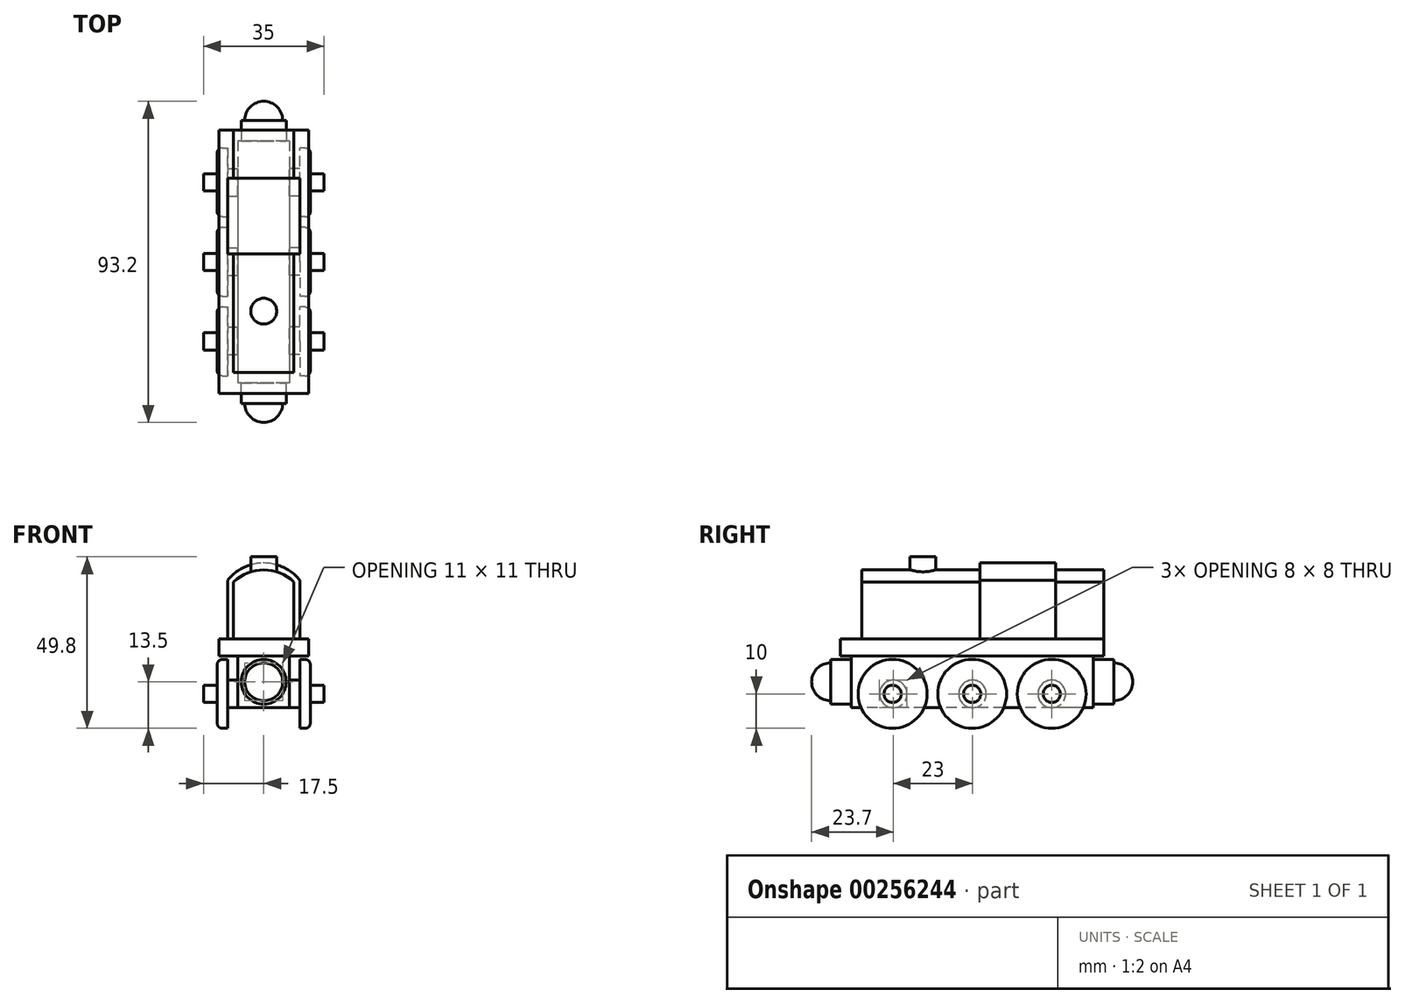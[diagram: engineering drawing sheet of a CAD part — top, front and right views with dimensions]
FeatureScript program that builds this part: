
annotation { "Feature Type Name" : "Feature", "Feature Type Description" : "" }
export const myFeature = defineFeature(function(context is Context, id is Id, definition is map)
    precondition{}
    {
        {
            var Q0;
            Q0=qCreatedBy(makeId("Front.planeOp"),FACE);
            var sketch = newSketch(context, id + "F0", { "sketchPlane" : qUnion([Q0])});
            skLineSegment(sketch, "E0.bottom", {"start": v(13, 2.5) * mm, "end": v(-13, 2.5) * mm});
            skLineSegment(sketch, "E0.top", {"start": v(13, -2.5) * mm, "end": v(-13, -2.5) * mm});
            skLineSegment(sketch, "E0.left", {"start": v(13, 2.5) * mm, "end": v(13, -2.5) * mm});
            skLineSegment(sketch, "E0.right", {"start": v(-13, 2.5) * mm, "end": v(-13, -2.5) * mm});
            skPoint(sketch, "E0.middle", {"position": v(0, 0) * mm});
            skSolve(sketch);
        }
        {
            var Q0;
            Q0 = qSketchRegion(id + "F0", true);
            extrude(context, id + "F1", {"entities" : qUnion([Q0]), "endBound" : BoundingType.SYMMETRIC, "depth" : 76.5 * mm});
        }
        {
            var Q0;
            Q0=makeQuery(id+"F1.opExtrude","SWEPT_FACE",FACE,{"disambiguationData":[OSD([sQuery(id+"F0.wireOp",EDGE,"E0.top")])]});
            var sketch = newSketch(context, id + "F2", { "sketchPlane" : qUnion([Q0])});
            skLineSegment(sketch, "E1.bottom", {"start": v(7.5, -35.1) * mm, "end": v(-7.5, -35.1) * mm});
            skLineSegment(sketch, "E1.top", {"start": v(7.5, 35.1) * mm, "end": v(-7.5, 35.1) * mm});
            skLineSegment(sketch, "E1.left", {"start": v(7.5, -35.1) * mm, "end": v(7.5, 35.1) * mm});
            skLineSegment(sketch, "E1.right", {"start": v(-7.5, -35.1) * mm, "end": v(-7.5, 35.1) * mm});
            skPoint(sketch, "E1.middle", {"position": v(0, 0) * mm});
            skSolve(sketch);
        }
        {
            var Q0;
            Q0 = qSketchRegion(id + "F2", true);
            extrude(context, id + "F3", {"entities" : qUnion([Q0]), "operationType" : NewBodyOperationType.ADD, "depth" : 15 * mm});
        }
        {
            var Q0;
            Q0=makeQuery(id+"F3.opExtrude","SWEPT_FACE",FACE,{"disambiguationData":[OSD([sQuery(id+"F2.wireOp",EDGE,"E1.top")])]});
            var sketch = newSketch(context, id + "F4", { "sketchPlane" : qUnion([Q0])});
            skPoint(sketch, "E2", {"position": v(-7.5, -10) * mm});
            skPoint(sketch, "E3", {"position": v(0, -10) * mm});
            skCircle(sketch, "E4", {"center": v(0, -10) * mm, "radius": 6.5 * mm});
            skSolve(sketch);
        }
        {
            var Q0;
            Q0 = qSketchRegion(id + "F4", true);
            extrude(context, id + "F5", {"entities" : qUnion([Q0]), "operationType" : NewBodyOperationType.ADD, "depth" : 6 * mm});
        }
        {
            var Q0;
            Q0=makeQuery(id+"F3.opExtrude","SWEPT_FACE",FACE,{"disambiguationData":[OSD([sQuery(id+"F2.wireOp",EDGE,"E1.bottom")])]});
            var sketch = newSketch(context, id + "F6", { "sketchPlane" : qUnion([Q0])});
            skCircle(sketch, "E5", {"center": v(0, -10) * mm, "radius": 6.5 * mm});
            skPoint(sketch, "E5.centerSnap0", {"position": v(-7.5, -10) * mm});
            skSolve(sketch);
        }
        {
            var Q0;
            Q0 = qSketchRegion(id + "F6", true);
            extrude(context, id + "F7", {"entities" : qUnion([Q0]), "operationType" : NewBodyOperationType.ADD, "depth" : 6 * mm});
        }
        {
            var Q0;
            Q0=makeQuery(id+"F7.opExtrude","CAP_FACE",FACE,{"disambiguationData":[OSD([sQuery(id+"F6.wireOp",EDGE,"E5")])],"isStart":false});
            var sketch = newSketch(context, id + "F8", { "sketchPlane" : qUnion([Q0])});
            skArc(sketch, "E6", {"start": v(0, -4.5) * mm, "mid": v(-5.5, -10) * mm, "end": v(0, -15.5) * mm});
            skLineSegment(sketch, "E7", {"start": v(0, -4.5) * mm, "end": v(0, -15.5) * mm});
            skSolve(sketch);
        }
        {
            var Q0;
            Q0=makeQuery(id+"F8.imprint","IMPRINT",FACE,{"disambiguationData":[TD([[makeQuery(id+"F8.imprint","IMPRINT",EDGE,{"derivedFrom":sQuery(id+"F8.wireOp",EDGE,"E6")}),1.0]])]});
            var Q1;
            Q1=sQuery(id+"F8.wireOp",EDGE,"E7");
            revolve(context, id + "F9", {"operationType" : NewBodyOperationType.ADD, "entities" : qUnion([Q0]), "axis" : qUnion([Q1]), "revolveType" : RevolveType.FULL});
        }
        {
            var Q0;
            Q0=makeQuery(id+"F5.opExtrude","CAP_FACE",FACE,{"disambiguationData":[OSD([sQuery(id+"F4.wireOp",EDGE,"E4")])],"isStart":false});
            var sketch = newSketch(context, id + "F10", { "sketchPlane" : qUnion([Q0])});
            skArc(sketch, "E8", {"start": v(0, -15.5) * mm, "mid": v(5.5, -10) * mm, "end": v(0, -4.5) * mm});
            skLineSegment(sketch, "E9", {"start": v(0, -4.5) * mm, "end": v(0, -15.5) * mm});
            skSolve(sketch);
        }
        {
            var Q0;
            Q0=makeQuery(id+"F10.imprint","IMPRINT",FACE,{"disambiguationData":[TD([[makeQuery(id+"F10.imprint","IMPRINT",EDGE,{"derivedFrom":sQuery(id+"F10.wireOp",EDGE,"E8")}),1.0]])]});
            var Q1;
            Q1=sQuery(id+"F10.wireOp",EDGE,"E9");
            revolve(context, id + "F11", {"operationType" : NewBodyOperationType.ADD, "entities" : qUnion([Q0]), "axis" : qUnion([Q1]), "revolveType" : RevolveType.FULL});
        }
        {
            var Q0;
            Q0=makeQuery(id+"F1.opExtrude","SWEPT_FACE",FACE,{"disambiguationData":[OSD([sQuery(id+"F0.wireOp",EDGE,"E0.bottom")])]});
            var sketch = newSketch(context, id + "F12", { "sketchPlane" : qUnion([Q0])});
            skLineSegment(sketch, "E10.bottom", {"start": v(10.5, 2.25) * mm, "end": v(-10.5, 2.25) * mm});
            skLineSegment(sketch, "E10.top", {"start": v(10.5, 24.25) * mm, "end": v(-10.5, 24.25) * mm});
            skLineSegment(sketch, "E10.left", {"start": v(10.5, 2.25) * mm, "end": v(10.5, 24.25) * mm});
            skLineSegment(sketch, "E10.right", {"start": v(-10.5, 2.25) * mm, "end": v(-10.5, 24.25) * mm});
            skLineSegment(sketch, "E11", {"start": v(-10.5, 13.25) * mm, "end": v(-13, 13.25) * mm, "construction": true});
            skLineSegment(sketch, "E12", {"start": v(10.5, 13.25) * mm, "end": v(13, 13.25) * mm, "construction": true});
            skSolve(sketch);
        }
        {
            var Q0;
            Q0 = qSketchRegion(id + "F12", true);
            extrude(context, id + "F13", {"entities" : qUnion([Q0]), "operationType" : NewBodyOperationType.ADD, "depth" : 17 * mm});
        }
        {
            var Q0;
            Q0=makeQuery(id+"F13.opExtrude","SWEPT_FACE",FACE,{"disambiguationData":[OSD([sQuery(id+"F12.wireOp",EDGE,"E10.top")])]});
            var sketch = newSketch(context, id + "F14", { "sketchPlane" : qUnion([Q0])});
            skArc(sketch, "E13", {"start": v(10.5, 19.5) * mm, "mid": v(0, 24.5) * mm, "end": v(-10.5, 19.5) * mm});
            skPoint(sketch, "E14", {"position": v(0, 24.5) * mm});
            skPoint(sketch, "E15", {"position": v(0, 19.5) * mm});
            skSolve(sketch);
        }
        {
            var Q0;
            Q0=makeQuery(id+"F14.imprint","IMPRINT",FACE,{"disambiguationData":[TD([[makeQuery(id+"F14.imprint","IMPRINT",EDGE,{"derivedFrom":sQuery(id+"F14.wireOp",EDGE,"E13")}),1.0]])]});
            extrude(context, id + "F15", {"entities" : qUnion([Q0]), "operationType" : NewBodyOperationType.ADD, "oppositeDirection" : true, "depth" : 22 * mm});
        }
        {
            var Q0;
            {var subQ0=sQuery(id+"F12.wireOp",EDGE,"E10.top");Q0=makeQuery(id+"F15.boolean.opBoolean","MERGE",FACE,{"derivedFrom":[makeQuery(id+"F13.opExtrude","SWEPT_FACE",FACE,{"disambiguationData":[OSD([subQ0])]}),makeQuery(id+"F15.opExtrude","CAP_FACE",FACE,{"disambiguationData":[OSD([subQ0,sQuery(id+"F14.wireOp",EDGE,"E13")])],"isStart":true})]});}
            var sketch = newSketch(context, id + "F16", { "sketchPlane" : qUnion([Q0])});
            skLineSegment(sketch, "E16.bottom", {"start": v(-8.75, 2.5) * mm, "end": v(8.75, 2.5) * mm});
            skLineSegment(sketch, "E16.top", {"start": v(-8.75, 19) * mm, "end": v(8.75, 19) * mm});
            skLineSegment(sketch, "E16.left", {"start": v(-8.75, 2.5) * mm, "end": v(-8.75, 19) * mm});
            skLineSegment(sketch, "E16.right", {"start": v(8.75, 2.5) * mm, "end": v(8.75, 19) * mm});
            skLineSegment(sketch, "E17", {"start": v(-8.75, 10.75) * mm, "end": v(-10.5, 10.75) * mm, "construction": true});
            skLineSegment(sketch, "E18", {"start": v(8.75, 10.75) * mm, "end": v(10.5, 10.75) * mm, "construction": true});
            skArc(sketch, "E19", {"start": v(8.75, 19) * mm, "mid": v(0, 22.5) * mm, "end": v(-8.75, 19) * mm});
            skPoint(sketch, "E20", {"position": v(0, 22.5) * mm});
            skPoint(sketch, "E21", {"position": v(0, 19) * mm});
            skSolve(sketch);
        }
        {
            var Q0;
            Q0 = qSketchRegion(id + "F16", true);
            extrude(context, id + "F17", {"entities" : qUnion([Q0]), "operationType" : NewBodyOperationType.ADD, "depth" : 14 * mm});
        }
        {
            var Q0;
            Q0=makeQuery(id+"F15.boolean.opBoolean","MERGE",FACE,{"derivedFrom":[makeQuery(id+"F13.opExtrude","SWEPT_FACE",FACE,{"disambiguationData":[OSD([sQuery(id+"F12.wireOp",EDGE,"E10.bottom")])]}),makeQuery(id+"F15.opExtrude","CAP_FACE",FACE,{"disambiguationData":[OSD([sQuery(id+"F12.wireOp",EDGE,"E10.top"),sQuery(id+"F14.wireOp",EDGE,"E13")])],"isStart":false})]});
            var sketch = newSketch(context, id + "F18", { "sketchPlane" : qUnion([Q0])});
            skPoint(sketch, "E22.0", {"position": v(-8.75, 2.5) * mm});
            skLineSegment(sketch, "E23.0", {"start": v(-8.75, 2.5) * mm, "end": v(-8.75, 19) * mm});
            skArc(sketch, "E24.0", {"start": v(-8.75, 19) * mm, "mid": v(0, 22.5) * mm, "end": v(8.75, 19) * mm});
            skLineSegment(sketch, "E25.0", {"start": v(8.75, 2.5) * mm, "end": v(8.75, 19) * mm});
            skLineSegment(sketch, "E26.bottom", {"start": v(-8.75, 2.5) * mm, "end": v(8.75, 2.5) * mm});
            skLineSegment(sketch, "E26.top", {"start": v(-8.75, 19) * mm, "end": v(8.75, 19) * mm});
            skPoint(sketch, "E27", {"position": v(0, 22.5) * mm});
            skArc(sketch, "E28", {"start": v(8.75, 19) * mm, "mid": v(0, 22.5) * mm, "end": v(-8.75, 19) * mm});
            skSolve(sketch);
        }
        {
            var Q0;
            Q0 = qSketchRegion(id + "F18", true);
            extrude(context, id + "F19", {"entities" : qUnion([Q0]), "operationType" : NewBodyOperationType.ADD, "depth" : 34.3 * mm});
        }
        {
            var Q0;
            Q0=makeQuery(id+"F1.opExtrude","SWEPT_FACE",FACE,{"disambiguationData":[OSD([sQuery(id+"F0.wireOp",EDGE,"E0.bottom")])]});
            var sketch = newSketch(context, id + "F20", { "sketchPlane" : qUnion([Q0])});
            skCircle(sketch, "E29", {"center": v(0, -14.3) * mm, "radius": 3.75 * mm});
            skPoint(sketch, "E30", {"position": v(3.75, -14.3) * mm});
            skPoint(sketch, "E31", {"position": v(0, -18.05) * mm});
            skPoint(sketch, "E32", {"position": v(8.75, -14.3) * mm});
            skPoint(sketch, "E33", {"position": v(0, -32.05) * mm});
            skSolve(sketch);
        }
        {
            var Q0;
            Q0 = qSketchRegion(id + "F20", true);
            extrude(context, id + "F21", {"entities" : qUnion([Q0]), "operationType" : NewBodyOperationType.ADD, "depth" : 23.8 * mm});
        }
        {
            var Q0;
            Q0=makeQuery(id+"F3.opExtrude","SWEPT_FACE",FACE,{"disambiguationData":[OSD([sQuery(id+"F2.wireOp",EDGE,"E1.right")])]});
            var sketch = newSketch(context, id + "F22", { "sketchPlane" : qUnion([Q0])});
            skCircle(sketch, "E34", {"center": v(-23.1, -13.5) * mm, "radius": 4 * mm});
            skPoint(sketch, "E35", {"position": v(-27.1, -13.5) * mm});
            skPoint(sketch, "E36", {"position": v(-23.1, -17.5) * mm});
            skPoint(sketch, "E37", {"position": v(-23.1, -9.5) * mm});
            skPoint(sketch, "E38", {"position": v(-35.1, -13.5) * mm});
            skPoint(sketch, "E39", {"position": v(-23.1, -2.5) * mm});
            skLineSegment(sketch, "E40", {"start": v(-35.1, -13.5) * mm, "end": v(35.1, -13.5) * mm, "construction": true});
            skCircle(sketch, "E41", {"center": v(-0.1, -13.5) * mm, "radius": 4 * mm});
            skPoint(sketch, "E42", {"position": v(-4.1, -13.5) * mm});
            skPoint(sketch, "E43", {"position": v(-19.1, -13.5) * mm});
            skPoint(sketch, "E44", {"position": v(0, -17.5) * mm});
            skPoint(sketch, "E44.positionSnap0", {"position": v(0, -13.5) * mm});
            skCircle(sketch, "E45", {"center": v(22.9, -13.5) * mm, "radius": 4 * mm});
            skPoint(sketch, "E46", {"position": v(18.9, -13.5) * mm});
            skPoint(sketch, "E47", {"position": v(3.9, -13.5) * mm});
            skSolve(sketch);
        }
        {
            var Q0;
            Q0 = qSketchRegion(id + "F22", true);
            extrude(context, id + "F23", {"entities" : qUnion([Q0]), "operationType" : NewBodyOperationType.ADD, "depth" : 3 * mm});
        }
        {
            var Q0;
            Q0=makeQuery(id+"F23.opExtrude","CAP_FACE",FACE,{"disambiguationData":[OSD([sQuery(id+"F22.wireOp",EDGE,"E34")])],"isStart":false});
            var sketch = newSketch(context, id + "F24", { "sketchPlane" : qUnion([Q0])});
            skCircle(sketch, "E48", {"center": v(-23.1, -13.5) * mm, "radius": 10 * mm});
            skCircle(sketch, "E49", {"center": v(0, -13.5) * mm, "radius": 10 * mm});
            skLineSegment(sketch, "E50", {"start": v(23.1, 0) * mm, "end": v(23.1, -13.5) * mm, "construction": true});
            skLineSegment(sketch, "E51", {"start": v(23.1, -13.5) * mm, "end": v(0, -13.5) * mm, "construction": true});
            skCircle(sketch, "E52", {"center": v(23.1, -13.5) * mm, "radius": 10 * mm});
            skPoint(sketch, "E53", {"position": v(0, -3.5) * mm});
            skPoint(sketch, "E54", {"position": v(0, 0) * mm});
            skPoint(sketch, "E55", {"position": v(10, -13.5) * mm});
            skPoint(sketch, "E56", {"position": v(13.1, -13.5) * mm});
            skPoint(sketch, "E57", {"position": v(-10, -13.5) * mm});
            skPoint(sketch, "E58", {"position": v(-13.1, -13.5) * mm});
            skPoint(sketch, "E59", {"position": v(23.1, -3.5) * mm});
            skPoint(sketch, "E60", {"position": v(23.1, 0) * mm});
            skSolve(sketch);
        }
        {
            var Q0;
            Q0 = qSketchRegion(id + "F24", true);
            extrude(context, id + "F25", {"entities" : qUnion([Q0]), "operationType" : NewBodyOperationType.ADD, "depth" : 3 * mm});
        }
        {
            var Q0;
            Q0=makeQuery(id+"F25.opExtrude","CAP_FACE",FACE,{"disambiguationData":[OSD([sQuery(id+"F24.wireOp",EDGE,"E48")])],"isStart":false});
            var sketch = newSketch(context, id + "F26", { "sketchPlane" : qUnion([Q0])});
            skCircle(sketch, "E61", {"center": v(-23.1, -13.5) * mm, "radius": 2.5 * mm});
            skCircle(sketch, "E62", {"center": v(0, -13.5) * mm, "radius": 2.5 * mm});
            skPoint(sketch, "E63", {"position": v(23.38, 0) * mm});
            skLineSegment(sketch, "E64", {"start": v(0, -13.5) * mm, "end": v(47.25, -13.5) * mm, "construction": true});
            skCircle(sketch, "E65", {"center": v(23.1, -13.5) * mm, "radius": 2.5 * mm});
            skPoint(sketch, "E66", {"position": v(20.6, -13.5) * mm});
            skPoint(sketch, "E67", {"position": v(2.5, -13.5) * mm});
            skLineSegment(sketch, "E68", {"start": v(0, -13.5) * mm, "end": v(-30.82, -13.5) * mm, "construction": true});
            skPoint(sketch, "E69", {"position": v(-2.5, -13.5) * mm});
            skPoint(sketch, "E70", {"position": v(-20.6, -13.5) * mm});
            skSolve(sketch);
        }
        {
            var Q0;
            Q0 = qSketchRegion(id + "F26", true);
            extrude(context, id + "F27", {"entities" : qUnion([Q0]), "operationType" : NewBodyOperationType.ADD, "depth" : 4 * mm});
        }
        {
            var Q0;
            Q0=makeQuery(id+"F1.opExtrude","SWEPT_BODY",BODY,{"disambiguationData":[OSD([sQuery(id+"F0.wireOp",EDGE,"E0.bottom"),sQuery(id+"F0.wireOp",EDGE,"E0.top"),sQuery(id+"F0.wireOp",EDGE,"E0.left"),sQuery(id+"F0.wireOp",EDGE,"E0.right")])]});
            var Q1;
            Q1=qCreatedBy(makeId("Right.planeOp"),FACE);
            mirror(context, id + "F28", {"operationType" : NewBodyOperationType.ADD, "entities" : qUnion([Q0]), "mirrorPlane" : qUnion([Q1])});
        }
        {
            var Q0;
            Q0=makeQuery(id+"F25.opExtrude","CAP_EDGE",EDGE,{"disambiguationData":[OSD([sQuery(id+"F24.wireOp",EDGE,"E48")])],"isStart":false});
            fillet(context, id + "F29", {"entities" : qUnion([Q0]), "radius" : 1.45 * mm, "tangentPropagation" : true, "allowEdgeOverflow" : false});
        }
        {
            var Q0;
            Q0=makeQuery(id+"F25.opExtrude","CAP_EDGE",EDGE,{"disambiguationData":[OSD([sQuery(id+"F24.wireOp",EDGE,"E52")])],"isStart":false});
            var Q1;
            Q1=makeQuery(id+"F25.opExtrude","CAP_EDGE",EDGE,{"disambiguationData":[OSD([sQuery(id+"F24.wireOp",EDGE,"E49")])],"isStart":false});
            var Q2;
            Q2=makeQuery(id+"F28.opPattern","COPY",EDGE,{"derivedFrom":makeQuery(id+"F25.opExtrude","CAP_EDGE",EDGE,{"disambiguationData":[OSD([sQuery(id+"F24.wireOp",EDGE,"E48")])],"isStart":false}),"instanceName":"1"});
            var Q3;
            Q3=makeQuery(id+"F28.opPattern","COPY",EDGE,{"derivedFrom":makeQuery(id+"F25.opExtrude","CAP_EDGE",EDGE,{"disambiguationData":[OSD([sQuery(id+"F24.wireOp",EDGE,"E49")])],"isStart":false}),"instanceName":"1"});
            var Q4;
            Q4=makeQuery(id+"F28.opPattern","COPY",EDGE,{"derivedFrom":makeQuery(id+"F25.opExtrude","CAP_EDGE",EDGE,{"disambiguationData":[OSD([sQuery(id+"F24.wireOp",EDGE,"E52")])],"isStart":false}),"instanceName":"1"});
            fillet(context, id + "F30", {"entities" : qUnion([Q0, Q1, Q2, Q3, Q4]), "radius" : 1.45 * mm, "tangentPropagation" : true, "allowEdgeOverflow" : false});
        }
    });
